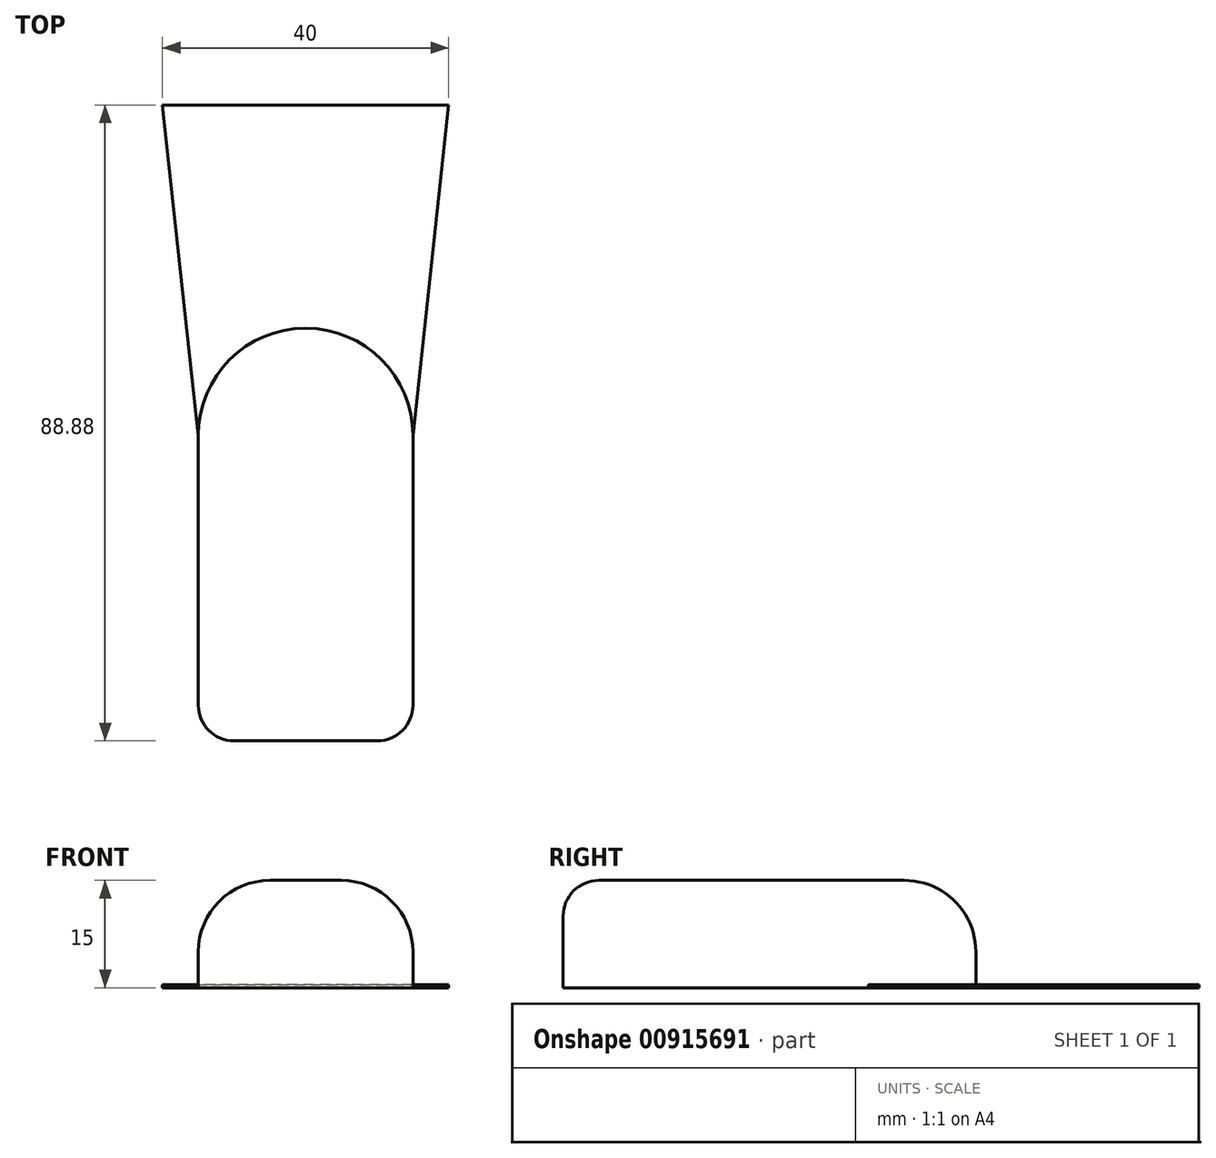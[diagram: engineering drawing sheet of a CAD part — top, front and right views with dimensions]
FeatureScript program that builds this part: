
annotation { "Feature Type Name" : "Feature", "Feature Type Description" : "" }
export const myFeature = defineFeature(function(context is Context, id is Id, definition is map)
    precondition{}
    {
        {
            var Q0;
            Q0=qCreatedBy(makeId("Top.planeOp"),FACE);
            var sketch = newSketch(context, id + "F0", { "sketchPlane" : qUnion([Q0])});
            skLineSegment(sketch, "E0", {"start": v(15, -30.23) * mm, "end": v(0, -30.23) * mm});
            skLineSegment(sketch, "E1", {"start": v(15, -72.91) * mm, "end": v(0, -72.91) * mm});
            skLineSegment(sketch, "E2", {"start": v(15, -30.23) * mm, "end": v(15, -72.91) * mm});
            skLineSegment(sketch, "E3", {"start": v(0, 0) * mm, "end": v(0, -72.91) * mm});
            skLineSegment(sketch, "E4.MirrorCS", {"start": v(-15, -72.91) * mm, "end": v(0, -72.91) * mm});
            skLineSegment(sketch, "E5.MirrorCS", {"start": v(-15, -30.23) * mm, "end": v(-15, -72.91) * mm});
            skLineSegment(sketch, "E6.MirrorCS", {"start": v(-15, -30.23) * mm, "end": v(0, -30.23) * mm});
            skArc(sketch, "E7", {"start": v(15, -30.23) * mm, "mid": v(0, -15.23) * mm, "end": v(-15, -30.23) * mm});
            skLineSegment(sketch, "E8", {"start": v(-20, 15.97) * mm, "end": v(20, 15.97) * mm});
            skLineSegment(sketch, "E9", {"start": v(-20, 15.97) * mm, "end": v(-15, -30.23) * mm});
            skLineSegment(sketch, "E10", {"start": v(20, 15.97) * mm, "end": v(15, -30.23) * mm});
            skSolve(sketch);
        }
        {
            var Q0;
            Q0=makeQuery(id+"F0.imprint","IMPRINT",FACE,{"disambiguationData":[TD([[makeQuery(id+"F0.imprint","IMPRINT",EDGE,{"derivedFrom":sQuery(id+"F0.wireOp",EDGE,"E8")}),-1.0]])]});
            extrude(context, id + "F1", {"entities" : qUnion([Q0]), "depth" : .4 * mm, "offsetDistance" : 25 * mm});
        }
        {
            var Q0;
            {var subQ0=sQuery(id+"F0.wireOp",EDGE,"E0");Q0=makeQuery(id+"F0.imprint","IMPRINT",FACE,{"disambiguationData":[TD([[makeQuery(id+"F0.imprint","IMPRINT",EDGE,{"derivedFrom":subQ0}),1.0]])]});}
            var Q1;
            {var subQ0=sQuery(id+"F0.wireOp",EDGE,"E0");Q1=makeQuery(id+"F0.imprint","IMPRINT",FACE,{"disambiguationData":[TD([[makeQuery(id+"F0.imprint","IMPRINT",EDGE,{"derivedFrom":subQ0}),-1.0]])]});}
            var Q2;
            {var subQ0=sQuery(id+"F0.wireOp",EDGE,"E6.MirrorCS");Q2=makeQuery(id+"F0.imprint","IMPRINT",FACE,{"disambiguationData":[TD([[makeQuery(id+"F0.imprint","IMPRINT",EDGE,{"derivedFrom":subQ0}),1.0]])]});}
            var Q3;
            {var subQ2=sQuery(id+"F0.wireOp",EDGE,"E4.MirrorCS");Q3=makeQuery(id+"F0.imprint","IMPRINT",FACE,{"disambiguationData":[TD([[makeQuery(id+"F0.imprint","IMPRINT",EDGE,{"derivedFrom":subQ2}),1.0]])]});}
            extrude(context, id + "F2", {"entities" : qUnion([Q0, Q1, Q2, Q3]), "operationType" : NewBodyOperationType.ADD, "depth" : 15 * mm, "offsetDistance" : 25 * mm});
        }
        {
            var Q0;
            Q0=makeQuery(id+"F2.opExtrude","CAP_EDGE",EDGE,{"disambiguationData":[OSD([sQuery(id+"F0.wireOp",EDGE,"E7")])],"isStart":false});
            fillet(context, id + "F3", {"entities" : qUnion([Q0]), "radius" : 10 * mm, "tangentPropagation" : true, "allowEdgeOverflow" : false});
        }
        {
            var Q0;
            Q0=makeQuery(id+"F3.opFillet","BLEND_EDGE",EDGE,{"blendedFrom":[makeQuery(id+"F2.opExtrude","CAP_EDGE",EDGE,{"disambiguationData":[OSD([sQuery(id+"F0.wireOp",EDGE,"E2")])],"isStart":false}),makeQuery(id+"F2.opExtrude","SWEPT_FACE",FACE,{"disambiguationData":[OSD([sQuery(id+"F0.wireOp",EDGE,"E1"),sQuery(id+"F0.wireOp",EDGE,"E4.MirrorCS")])]})],"blendedInto":[makeQuery(id+"F2.opExtrude","SWEPT_FACE",FACE,{"disambiguationData":[OSD([sQuery(id+"F0.wireOp",EDGE,"E1"),sQuery(id+"F0.wireOp",EDGE,"E4.MirrorCS")])]})]});
            fillet(context, id + "F4", {"entities" : qUnion([Q0]), "radius" : 5 * mm, "tangentPropagation" : true, "allowEdgeOverflow" : false});
        }
    });
